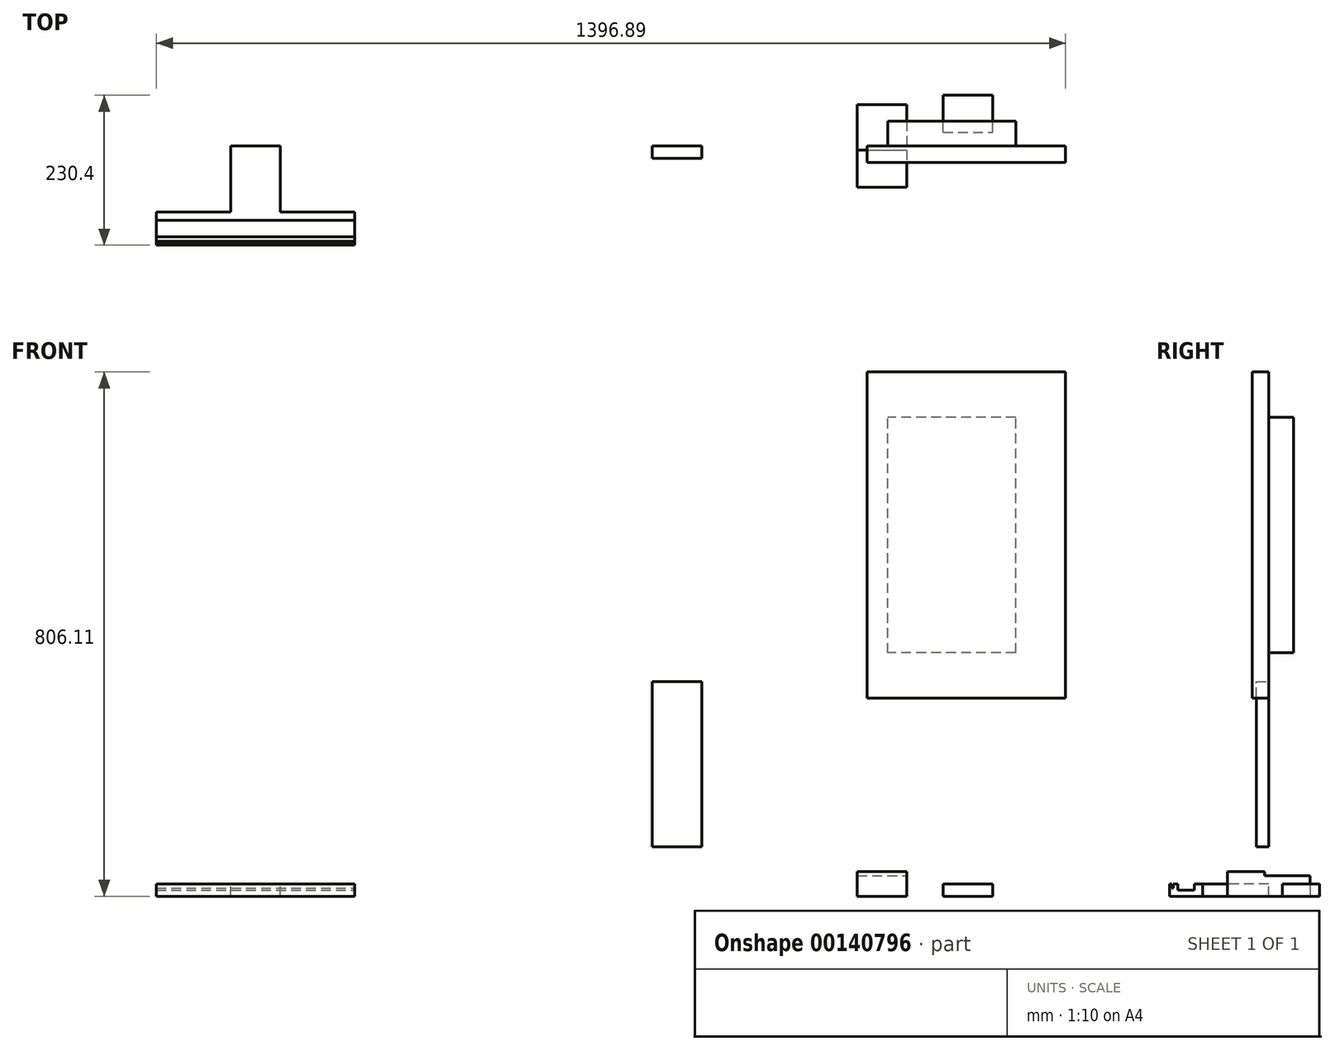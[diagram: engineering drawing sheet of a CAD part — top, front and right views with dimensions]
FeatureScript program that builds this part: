
annotation { "Feature Type Name" : "Feature", "Feature Type Description" : "" }
export const myFeature = defineFeature(function(context is Context, id is Id, definition is map)
    precondition{}
    {
        {
            var Q0;
            Q0=qCreatedBy(makeId("Top.planeOp"),FACE);
            var sketch = newSketch(context, id + "F0", { "sketchPlane" : qUnion([Q0])});
            skLineSegment(sketch, "E0.bottom", {"start": v(38.1, 63.5) * mm, "end": v(-38.1, 63.5) * mm});
            skLineSegment(sketch, "E0.top", {"start": v(38.1, -63.5) * mm, "end": v(-38.1, -63.5) * mm});
            skLineSegment(sketch, "E0.left", {"start": v(38.1, 63.5) * mm, "end": v(38.1, -63.5) * mm});
            skLineSegment(sketch, "E0.right", {"start": v(-38.1, 63.5) * mm, "end": v(-38.1, -63.5) * mm});
            skPoint(sketch, "E0.middle", {"position": v(0, 0) * mm});
            skSolve(sketch);
        }
        {
            var Q0;
            Q0 = qSketchRegion(id + "F0", true);
            extrude(context, id + "F1", {"entities" : qUnion([Q0]), "depth" : 38.1 * mm});
        }
        {
            var Q0;
            Q0=makeQuery(id+"F1.opExtrude","SWEPT_FACE",FACE,{"disambiguationData":[OSD([sQuery(id+"F0.wireOp",EDGE,"E0.left")])]});
            var sketch = newSketch(context, id + "F2", { "sketchPlane" : qUnion([Q0])});
            skLineSegment(sketch, "E1.bottom", {"start": v(63.5, 38.1) * mm, "end": v(-6.35, 38.1) * mm});
            skLineSegment(sketch, "E1.top", {"start": v(63.5, 31.75) * mm, "end": v(-6.35, 31.75) * mm});
            skLineSegment(sketch, "E1.left", {"start": v(63.5, 38.1) * mm, "end": v(63.5, 31.75) * mm});
            skLineSegment(sketch, "E1.right", {"start": v(-6.35, 38.1) * mm, "end": v(-6.35, 31.75) * mm});
            skSolve(sketch);
        }
        {
            var Q0;
            Q0 = qSketchRegion(id + "F2", true);
            var Q1;
            Q1=makeQuery(id+"F1.opExtrude","SWEPT_FACE",FACE,{"disambiguationData":[OSD([sQuery(id+"F0.wireOp",EDGE,"E0.right")])]});
            extrude(context, id + "F3", {"entities" : qUnion([Q0]), "operationType" : NewBodyOperationType.ADD, "endBound" : BoundingType.UP_TO_SURFACE, "oppositeDirection" : true, "endBoundEntityFace" : qUnion([Q1]), "depth" : 25.4 * mm});
        }
        {
            var Q0;
            Q0 = qSketchRegion(id + "F2", true);
            extrude(context, id + "F4", {"entities" : qUnion([Q0]), "operationType" : NewBodyOperationType.REMOVE, "endBound" : BoundingType.UP_TO_NEXT, "oppositeDirection" : true, "depth" : 25.4 * mm});
        }
        {
            var Q0;
            Q0=qCreatedBy(makeId("Top.planeOp"),FACE);
            var sketch = newSketch(context, id + "F5", { "sketchPlane" : qUnion([Q0])});
            skLineSegment(sketch, "E2.bottom", {"start": v(93.85, 20.85) * mm, "end": v(170.05, 20.85) * mm});
            skLineSegment(sketch, "E2.top", {"start": v(93.85, 78) * mm, "end": v(170.05, 78) * mm});
            skLineSegment(sketch, "E2.left", {"start": v(93.85, 20.85) * mm, "end": v(93.85, 78) * mm});
            skLineSegment(sketch, "E2.right", {"start": v(170.05, 20.85) * mm, "end": v(170.05, 78) * mm});
            skSolve(sketch);
        }
        {
            var Q0;
            Q0 = qSketchRegion(id + "F5", true);
            extrude(context, id + "F6", {"entities" : qUnion([Q0]), "depth" : 19.05 * mm});
        }
        {
            var Q0;
            Q0=qCreatedBy(makeId("Top.planeOp"),FACE);
            var sketch = newSketch(context, id + "F7", { "sketchPlane" : qUnion([Q0])});
            skLineSegment(sketch, "E3.bottom", {"start": v(-810.44, -152.4) * mm, "end": v(-1115.24, -152.4) * mm});
            skLineSegment(sketch, "E3.top", {"start": v(-810.44, 0) * mm, "end": v(-1115.24, 0) * mm});
            skLineSegment(sketch, "E3.left", {"start": v(-810.44, -152.4) * mm, "end": v(-810.44, 0) * mm});
            skLineSegment(sketch, "E3.right", {"start": v(-1115.24, -152.4) * mm, "end": v(-1115.24, 0) * mm});
            skSolve(sketch);
        }
        {
            var Q0;
            Q0 = qSketchRegion(id + "F7", true);
            extrude(context, id + "F8", {"entities" : qUnion([Q0]), "depth" : 19.05 * mm});
        }
        {
            var Q0;
            Q0=makeQuery(id+"F8.opExtrude","CAP_FACE",FACE,{"disambiguationData":[OSD([sQuery(id+"F7.wireOp",EDGE,"E3.bottom"),sQuery(id+"F7.wireOp",EDGE,"E3.top"),sQuery(id+"F7.wireOp",EDGE,"E3.left"),sQuery(id+"F7.wireOp",EDGE,"E3.right")])],"isStart":false});
            var sketch = newSketch(context, id + "F9", { "sketchPlane" : qUnion([Q0])});
            skLineSegment(sketch, "E4.bottom", {"start": v(-810.44, 0) * mm, "end": v(-924.74, 0) * mm});
            skLineSegment(sketch, "E4.top", {"start": v(-810.44, -101.6) * mm, "end": v(-924.74, -101.6) * mm});
            skLineSegment(sketch, "E4.left", {"start": v(-810.44, 0) * mm, "end": v(-810.44, -101.6) * mm});
            skLineSegment(sketch, "E4.right", {"start": v(-924.74, 0) * mm, "end": v(-924.74, -101.6) * mm});
            skLineSegment(sketch, "E5.bottom", {"start": v(-1115.24, 0) * mm, "end": v(-1000.94, 0) * mm});
            skLineSegment(sketch, "E5.top", {"start": v(-1115.24, -101.6) * mm, "end": v(-1000.94, -101.6) * mm});
            skLineSegment(sketch, "E5.left", {"start": v(-1115.24, 0) * mm, "end": v(-1115.24, -101.6) * mm});
            skLineSegment(sketch, "E5.right", {"start": v(-1000.94, 0) * mm, "end": v(-1000.94, -101.6) * mm});
            skSolve(sketch);
        }
        {
            var Q0;
            Q0 = qSketchRegion(id + "F9", true);
            extrude(context, id + "F10", {"entities" : qUnion([Q0]), "operationType" : NewBodyOperationType.REMOVE, "endBound" : BoundingType.UP_TO_NEXT, "oppositeDirection" : true, "depth" : 25.4 * mm});
        }
        {
            var Q0;
            Q0=makeQuery(id+"F8.opExtrude","SWEPT_FACE",FACE,{"disambiguationData":[OSD([sQuery(id+"F7.wireOp",EDGE,"E3.left")])]});
            var sketch = newSketch(context, id + "F11", { "sketchPlane" : qUnion([Q0])});
            skLineSegment(sketch, "E6.bottom", {"start": v(-149.22, 19.05) * mm, "end": v(-146.68, 19.05) * mm});
            skLineSegment(sketch, "E6.top", {"start": v(-149.22, 12.7) * mm, "end": v(-146.68, 12.7) * mm});
            skLineSegment(sketch, "E6.left", {"start": v(-149.22, 19.05) * mm, "end": v(-149.22, 12.7) * mm});
            skLineSegment(sketch, "E6.right", {"start": v(-146.68, 19.05) * mm, "end": v(-146.68, 12.7) * mm});
            skLineSegment(sketch, "E7.bottom", {"start": v(-139.7, 19.05) * mm, "end": v(-114.3, 19.05) * mm});
            skLineSegment(sketch, "E7.top", {"start": v(-139.7, 9.53) * mm, "end": v(-114.3, 9.53) * mm});
            skLineSegment(sketch, "E7.left", {"start": v(-139.7, 19.05) * mm, "end": v(-139.7, 9.53) * mm});
            skLineSegment(sketch, "E7.right", {"start": v(-114.3, 19.05) * mm, "end": v(-114.3, 9.53) * mm});
            skSolve(sketch);
        }
        {
            var Q0;
            Q0 = qSketchRegion(id + "F11", true);
            extrude(context, id + "F12", {"entities" : qUnion([Q0]), "operationType" : NewBodyOperationType.REMOVE, "endBound" : BoundingType.UP_TO_NEXT, "oppositeDirection" : true, "depth" : 25.4 * mm});
        }
        {
            var Q0;
            Q0=qCreatedBy(makeId("Front.planeOp"),FACE);
            var sketch = newSketch(context, id + "F13", { "sketchPlane" : qUnion([Q0])});
            skLineSegment(sketch, "E8.bottom", {"start": v(-277.3, 75.75) * mm, "end": v(-353.5, 75.75) * mm});
            skLineSegment(sketch, "E8.top", {"start": v(-277.3, 329.75) * mm, "end": v(-353.5, 329.75) * mm});
            skLineSegment(sketch, "E8.left", {"start": v(-277.3, 75.75) * mm, "end": v(-277.3, 329.75) * mm});
            skLineSegment(sketch, "E8.right", {"start": v(-353.5, 75.75) * mm, "end": v(-353.5, 329.75) * mm});
            skSolve(sketch);
        }
        {
            var Q0;
            Q0 = qSketchRegion(id + "F13", true);
            extrude(context, id + "F14", {"entities" : qUnion([Q0]), "depth" : 19.05 * mm});
        }
        {
            var Q0;
            Q0=qCreatedBy(makeId("Front.planeOp"),FACE);
            var sketch = newSketch(context, id + "F15", { "sketchPlane" : qUnion([Q0])});
            skLineSegment(sketch, "E9.bottom", {"start": v(-23.15, 304.46) * mm, "end": v(281.65, 304.46) * mm});
            skLineSegment(sketch, "E9.top", {"start": v(-23.15, 806.11) * mm, "end": v(281.65, 806.11) * mm});
            skLineSegment(sketch, "E9.left", {"start": v(-23.15, 304.46) * mm, "end": v(-23.15, 806.11) * mm});
            skLineSegment(sketch, "E9.right", {"start": v(281.65, 304.46) * mm, "end": v(281.65, 806.11) * mm});
            skSolve(sketch);
        }
        {
            var Q0;
            Q0 = qSketchRegion(id + "F15", true);
            extrude(context, id + "F16", {"entities" : qUnion([Q0]), "depth" : 25.4 * mm});
        }
        {
            var Q0;
            Q0=makeQuery(id+"F16.opExtrude","CAP_FACE",FACE,{"disambiguationData":[OSD([sQuery(id+"F15.wireOp",EDGE,"E9.bottom"),sQuery(id+"F15.wireOp",EDGE,"E9.top"),sQuery(id+"F15.wireOp",EDGE,"E9.left"),sQuery(id+"F15.wireOp",EDGE,"E9.right")])],"isStart":true});
            var sketch = newSketch(context, id + "F17", { "sketchPlane" : qUnion([Q0])});
            skLineSegment(sketch, "E10.bottom", {"start": v(-205.45, 374.31) * mm, "end": v(-8.6, 374.31) * mm});
            skLineSegment(sketch, "E10.top", {"start": v(-205.45, 736.26) * mm, "end": v(-8.6, 736.26) * mm});
            skLineSegment(sketch, "E10.left", {"start": v(-205.45, 374.31) * mm, "end": v(-205.45, 736.26) * mm});
            skLineSegment(sketch, "E10.right", {"start": v(-8.6, 374.31) * mm, "end": v(-8.6, 736.26) * mm});
            skSolve(sketch);
        }
        {
            var Q0;
            Q0 = qSketchRegion(id + "F17", true);
            extrude(context, id + "F18", {"entities" : qUnion([Q0]), "operationType" : NewBodyOperationType.ADD, "depth" : 38.1 * mm});
        }
    });
